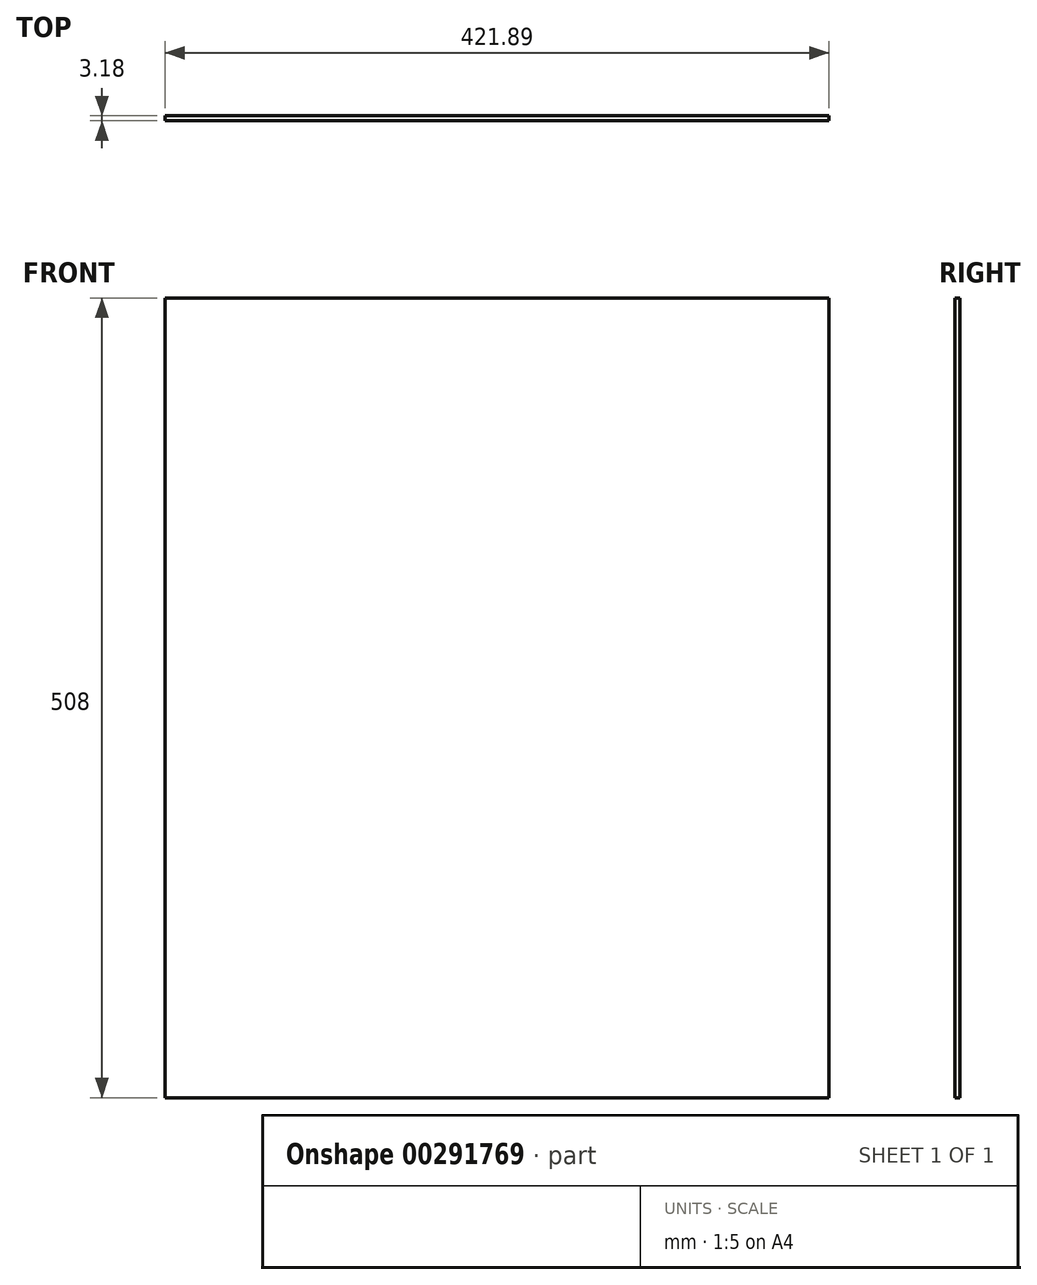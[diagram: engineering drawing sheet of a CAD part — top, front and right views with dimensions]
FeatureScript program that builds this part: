
annotation { "Feature Type Name" : "Feature", "Feature Type Description" : "" }
export const myFeature = defineFeature(function(context is Context, id is Id, definition is map)
    precondition{}
    {
        {
            var Q0;
            Q0=qCreatedBy(makeId("Front.planeOp"),FACE);
            var sketch = newSketch(context, id + "F0", { "sketchPlane" : qUnion([Q0])});
            skLineSegment(sketch, "E0.bottom", {"start": v(-211.76, -125.17) * mm, "end": v(210.13, -125.17) * mm});
            skLineSegment(sketch, "E0.top", {"start": v(-211.76, -633.17) * mm, "end": v(210.13, -633.17) * mm});
            skLineSegment(sketch, "E0.left", {"start": v(-211.76, -125.17) * mm, "end": v(-211.76, -633.17) * mm});
            skLineSegment(sketch, "E0.right", {"start": v(210.13, -125.17) * mm, "end": v(210.13, -633.17) * mm});
            skSolve(sketch);
        }
        {
            var Q0;
            Q0 = qSketchRegion(id + "F0", true);
            extrude(context, id + "F1", {"entities" : qUnion([Q0]), "endBound" : BoundingType.SYMMETRIC, "depth" : 3.17 * mm});
        }
    });
